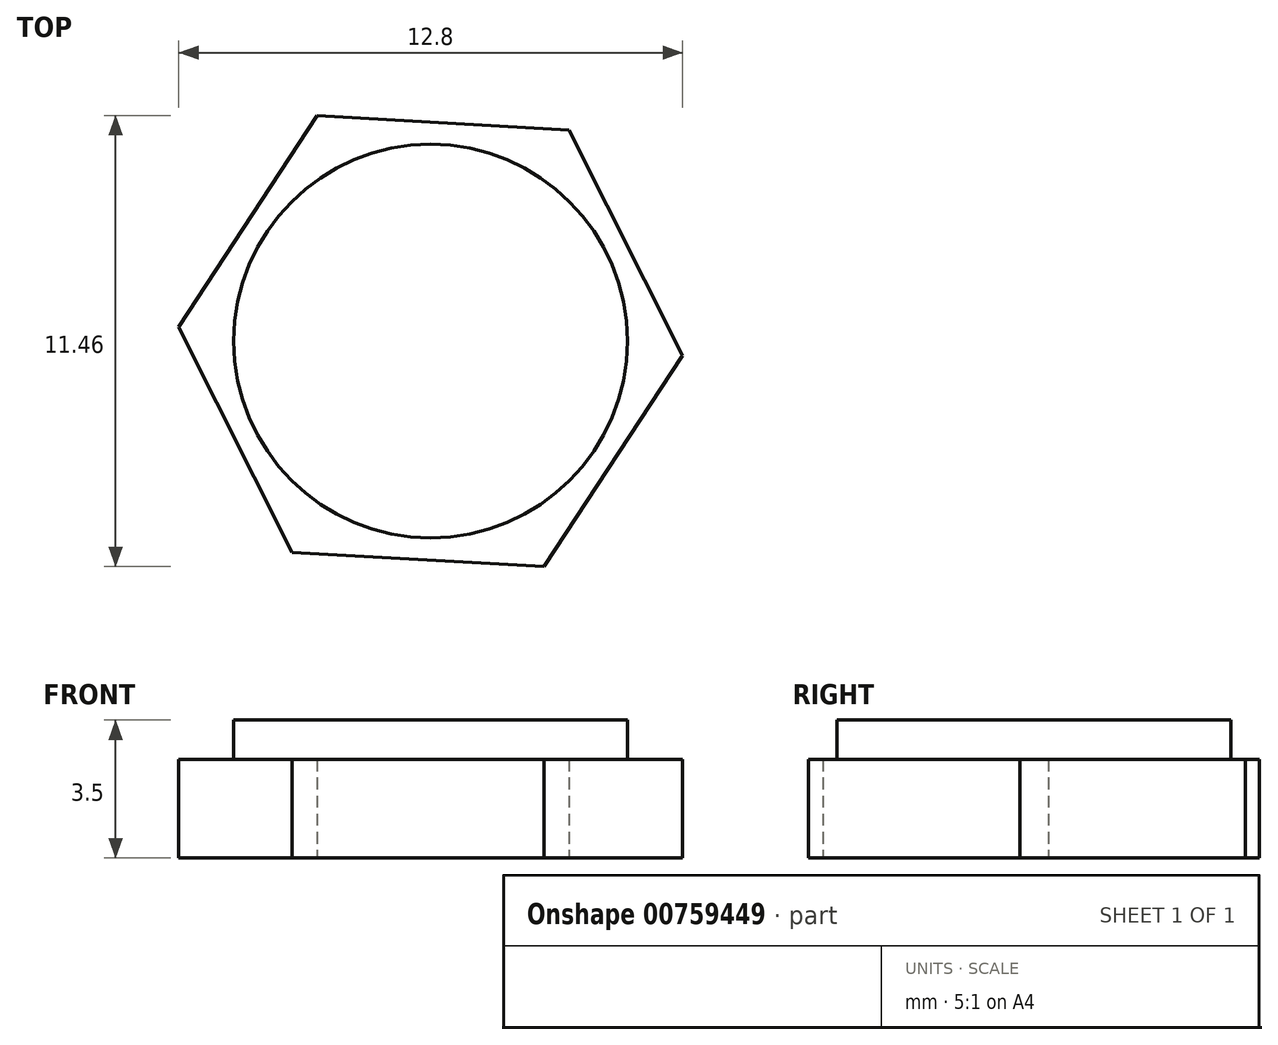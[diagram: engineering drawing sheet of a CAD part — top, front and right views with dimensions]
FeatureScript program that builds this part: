
annotation { "Feature Type Name" : "Feature", "Feature Type Description" : "" }
export const myFeature = defineFeature(function(context is Context, id is Id, definition is map)
    precondition{}
    {
        {
            var Q0;
            Q0=qCreatedBy(makeId("Top.planeOp"),FACE);
            var sketch = newSketch(context, id + "F0", { "sketchPlane" : qUnion([Q0])});
            skCircle(sketch, "E0", {"center": v(0, 0) * mm, "radius": 5 * mm});
            skPoint(sketch, "E1.end.orphan", {"position": v(0, 10.93) * mm});
            skPoint(sketch, "E2.end.orphan", {"position": v(7.25, -5.47) * mm});
            skPoint(sketch, "E3.end.orphan", {"position": v(0, -12.04) * mm});
            skPoint(sketch, "E4.end.orphan", {"position": v(-8.32, -5.47) * mm});
            skCircle(sketch, "E5.cCircle", {"center": v(0, 0) * mm, "radius": 6.41 * mm, "construction": true});
            skLineSegment(sketch, "E5.0", {"start": v(3.52, 5.36) * mm, "end": v(6.4, -0.36) * mm});
            skLineSegment(sketch, "E5.1", {"start": v(6.4, -0.36) * mm, "end": v(2.89, -5.73) * mm});
            skLineSegment(sketch, "E5.2", {"start": v(2.89, -5.73) * mm, "end": v(-3.52, -5.36) * mm});
            skLineSegment(sketch, "E5.3", {"start": v(-3.52, -5.36) * mm, "end": v(-6.4, 0.36) * mm});
            skLineSegment(sketch, "E5.4", {"start": v(-6.4, 0.36) * mm, "end": v(-2.89, 5.73) * mm});
            skLineSegment(sketch, "E5.5", {"start": v(-2.89, 5.73) * mm, "end": v(3.52, 5.36) * mm});
            skSolve(sketch);
        }
        {
            var Q0;
            Q0 = qSketchRegion(id + "F0", true);
            var Q1;
            Q1=makeQuery(id+"F0.imprint","IMPRINT",FACE,{"disambiguationData":[TD([[makeQuery(id+"F0.imprint","IMPRINT",EDGE,{"derivedFrom":sQuery(id+"F0.wireOp",EDGE,"E0")}),1.0]])]});
            extrude(context, id + "F1", {"entities" : qUnion([Q0, Q1]), "depth" : 2.5 * mm, "offsetDistance" : 25 * mm});
        }
        {
            var Q0;
            Q0=makeQuery(id+"F0.imprint","IMPRINT",FACE,{"disambiguationData":[TD([[makeQuery(id+"F0.imprint","IMPRINT",EDGE,{"derivedFrom":sQuery(id+"F0.wireOp",EDGE,"E0")}),1.0]])]});
            extrude(context, id + "F2", {"entities" : qUnion([Q0]), "operationType" : NewBodyOperationType.ADD, "depth" : 3.5 * mm, "offsetDistance" : 25 * mm});
        }
    });
